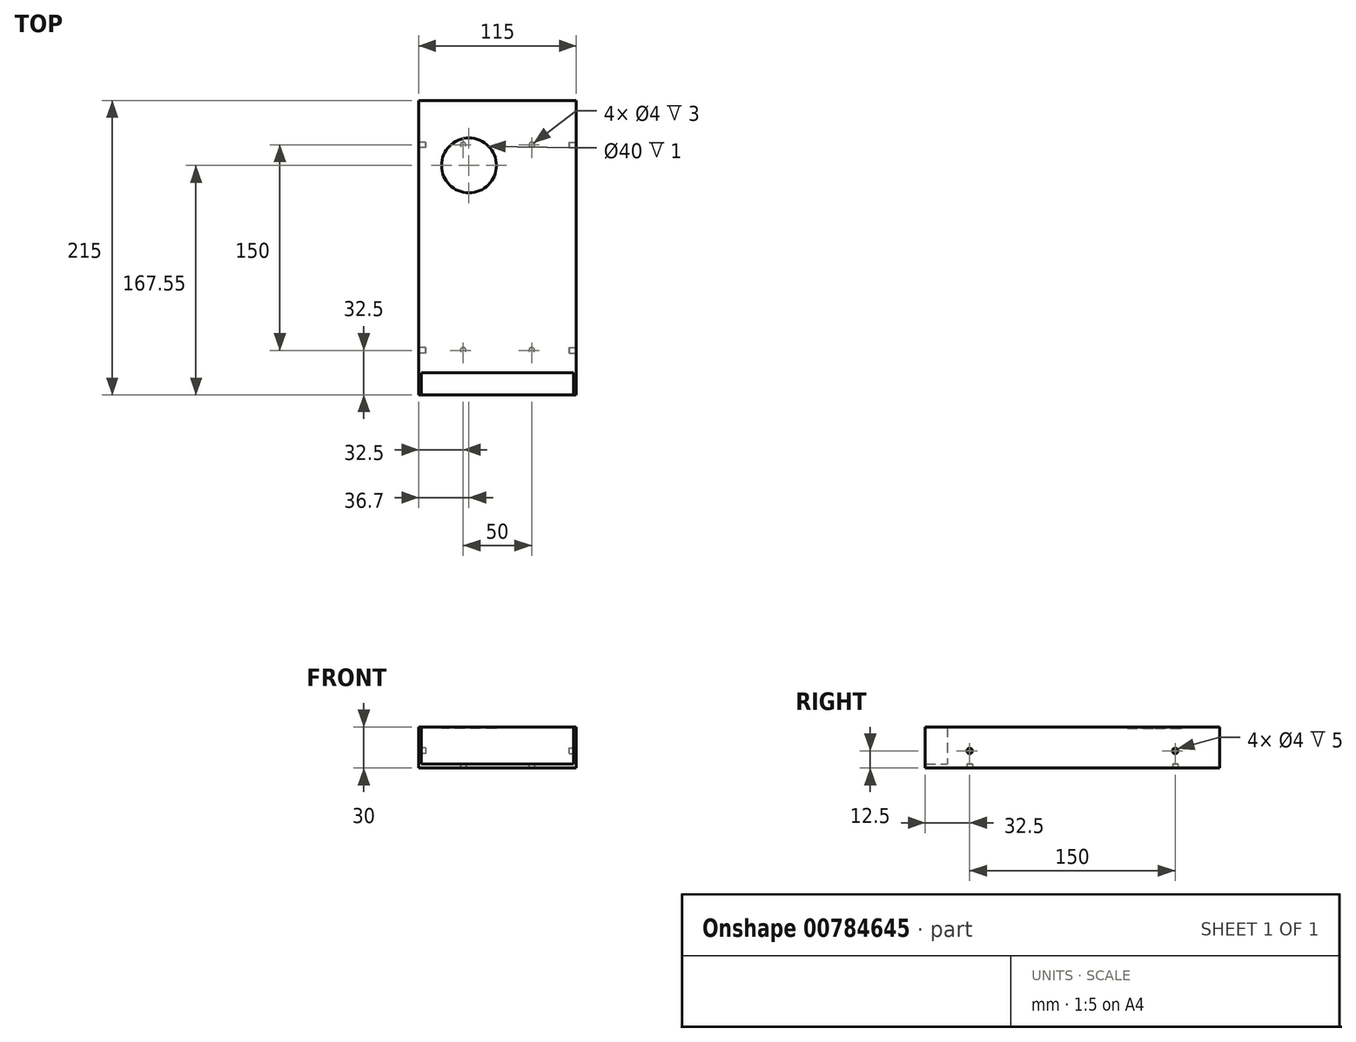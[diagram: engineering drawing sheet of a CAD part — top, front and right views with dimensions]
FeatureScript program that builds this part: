
annotation { "Feature Type Name" : "Feature", "Feature Type Description" : "" }
export const myFeature = defineFeature(function(context is Context, id is Id, definition is map)
    precondition{}
    {
        {
            var Q0;
            Q0=qCreatedBy(makeId("Top.planeOp"),FACE);
            var sketch = newSketch(context, id + "F0", { "sketchPlane" : qUnion([Q0])});
            skLineSegment(sketch, "E0.bottom", {"start": v(57.5, -107.5) * mm, "end": v(-57.5, -107.5) * mm});
            skLineSegment(sketch, "E0.top", {"start": v(57.5, 107.5) * mm, "end": v(-57.5, 107.5) * mm});
            skLineSegment(sketch, "E0.left", {"start": v(57.5, -107.5) * mm, "end": v(57.5, 107.5) * mm});
            skLineSegment(sketch, "E0.right", {"start": v(-57.5, -107.5) * mm, "end": v(-57.5, 107.5) * mm});
            skPoint(sketch, "E0.middle", {"position": v(0, 0) * mm});
            skLineSegment(sketch, "E1", {"start": v(-57.5, -91.25) * mm, "end": v(57.5, -91.25) * mm});
            skLineSegment(sketch, "E2", {"start": v(-55.5, -91.25) * mm, "end": v(-55.5, -107.5) * mm});
            skLineSegment(sketch, "E3", {"start": v(55.5, -91.25) * mm, "end": v(55.5, -107.5) * mm});
            skSolve(sketch);
        }
        {
            var Q0;
            Q0=makeQuery(id+"F0.imprint","IMPRINT",FACE,{"disambiguationData":[TD([[makeQuery(id+"F0.imprint","IMPRINT",EDGE,{"derivedFrom":sQuery(id+"F0.wireOp",EDGE,"E0.bottom")}),-1.0]])]});
            var Q1;
            {var subQ1=sQuery(id+"F0.wireOp",EDGE,"E0.top");Q1=makeQuery(id+"F0.imprint","IMPRINT",FACE,{"disambiguationData":[TD([[makeQuery(id+"F0.imprint","IMPRINT",EDGE,{"derivedFrom":subQ1}),1.0]])]});}
            extrude(context, id + "F1", {"entities" : qUnion([Q0, Q1]), "depth" : 3 * mm, "offsetDistance" : 25 * mm});
        }
        {
            var Q0;
            {var subQ3=sQuery(id+"F0.wireOp",EDGE,"E3");Q0=makeQuery(id+"F0.imprint","IMPRINT",FACE,{"disambiguationData":[TD([[makeQuery(id+"F0.imprint","IMPRINT",EDGE,{"derivedFrom":subQ3}),1.0]])]});}
            var Q1;
            {var subQ3=sQuery(id+"F0.wireOp",EDGE,"E2");Q1=makeQuery(id+"F0.imprint","IMPRINT",FACE,{"disambiguationData":[TD([[makeQuery(id+"F0.imprint","IMPRINT",EDGE,{"derivedFrom":subQ3}),-1.0]])]});}
            var Q2;
            {var subQ1=sQuery(id+"F0.wireOp",EDGE,"E0.top");Q2=makeQuery(id+"F0.imprint","IMPRINT",FACE,{"disambiguationData":[TD([[makeQuery(id+"F0.imprint","IMPRINT",EDGE,{"derivedFrom":subQ1}),1.0]])]});}
            extrude(context, id + "F2", {"entities" : qUnion([Q0, Q1, Q2]), "operationType" : NewBodyOperationType.ADD, "depth" : 30 * mm, "offsetDistance" : 25 * mm});
        }
        {
            var Q0;
            {var subQ0=sQuery(id+"F0.wireOp",EDGE,"E0.left");Q0=makeQuery(id+"F2.boolean.opBoolean","MERGE",FACE,{"derivedFrom":[makeQuery(id+"F1.opExtrude","SWEPT_FACE",FACE,{"disambiguationData":[OSD([subQ0])]}),makeQuery(id+"F2.opExtrude","SWEPT_FACE",FACE,{"disambiguationData":[OSD([subQ0])]})]});}
            var sketch = newSketch(context, id + "F3", { "sketchPlane" : qUnion([Q0])});
            skCircle(sketch, "E4", {"center": v(-75, 12.5) * mm, "radius": 2 * mm});
            skCircle(sketch, "E5", {"center": v(75, 12.5) * mm, "radius": 2 * mm});
            skSolve(sketch);
        }
        {
            var Q0;
            Q0 = qSketchRegion(id + "F3", true);
            extrude(context, id + "F4", {"entities" : qUnion([Q0]), "operationType" : NewBodyOperationType.REMOVE, "oppositeDirection" : true, "depth" : 5 * mm, "offsetDistance" : 25 * mm});
        }
        {
            var Q0;
            Q0=makeQuery(id+"F1.opExtrude","CAP_FACE",FACE,{"disambiguationData":[OSD([sQuery(id+"F0.wireOp",EDGE,"E0.bottom"),sQuery(id+"F0.wireOp",EDGE,"E0.top"),sQuery(id+"F0.wireOp",EDGE,"E0.left"),sQuery(id+"F0.wireOp",EDGE,"E0.right")])],"isStart":true});
            var sketch = newSketch(context, id + "F5", { "sketchPlane" : qUnion([Q0])});
            skCircle(sketch, "E6", {"center": v(25, 75) * mm, "radius": 2 * mm});
            skCircle(sketch, "E7", {"center": v(25, -75) * mm, "radius": 2 * mm});
            skPoint(sketch, "E8.0", {"position": v(57.5, 75) * mm});
            skPoint(sketch, "E9.0", {"position": v(57.5, -75) * mm});
            skCircle(sketch, "E10.MirrorC", {"center": v(-25, 75) * mm, "radius": 2 * mm});
            skCircle(sketch, "E11.MirrorC", {"center": v(-25, -75) * mm, "radius": 2 * mm});
            skSolve(sketch);
        }
        {
            var Q0;
            Q0 = qSketchRegion(id + "F5", true);
            extrude(context, id + "F6", {"entities" : qUnion([Q0]), "operationType" : NewBodyOperationType.REMOVE, "oppositeDirection" : true, "depth" : 3 * mm, "offsetDistance" : 25 * mm});
        }
        {
            var Q0;
            {var subQ0=sQuery(id+"F0.wireOp",EDGE,"E0.right");Q0=makeQuery(id+"F2.boolean.opBoolean","MERGE",FACE,{"derivedFrom":[makeQuery(id+"F1.opExtrude","SWEPT_FACE",FACE,{"disambiguationData":[OSD([subQ0])]}),makeQuery(id+"F2.opExtrude","SWEPT_FACE",FACE,{"disambiguationData":[OSD([subQ0])]})]});}
            var sketch = newSketch(context, id + "F7", { "sketchPlane" : qUnion([Q0])});
            skCircle(sketch, "E12", {"center": v(-75, 12.5) * mm, "radius": 2 * mm});
            skCircle(sketch, "E13", {"center": v(75, 12.5) * mm, "radius": 2 * mm});
            skSolve(sketch);
        }
        {
            var Q0;
            Q0 = qSketchRegion(id + "F7", true);
            extrude(context, id + "F8", {"entities" : qUnion([Q0]), "operationType" : NewBodyOperationType.REMOVE, "oppositeDirection" : true, "depth" : 5 * mm, "offsetDistance" : 25 * mm});
        }
        {
            var Q0;
            Q0=makeQuery(id+"F2.opExtrude","CAP_FACE",FACE,{"disambiguationData":[OSD([sQuery(id+"F0.wireOp",EDGE,"E0.bottom"),sQuery(id+"F0.wireOp",EDGE,"E0.top"),sQuery(id+"F0.wireOp",EDGE,"E0.left"),sQuery(id+"F0.wireOp",EDGE,"E0.right"),sQuery(id+"F0.wireOp",EDGE,"E1"),sQuery(id+"F0.wireOp",EDGE,"E2"),sQuery(id+"F0.wireOp",EDGE,"E3")])],"isStart":false});
            var sketch = newSketch(context, id + "F9", { "sketchPlane" : qUnion([Q0])});
            skCircle(sketch, "E14", {"center": v(-20.8, 60.05) * mm, "radius": 20 * mm});
            skSolve(sketch);
        }
        {
            var Q0;
            Q0 = qSketchRegion(id + "F9", true);
            extrude(context, id + "F10", {"entities" : qUnion([Q0]), "operationType" : NewBodyOperationType.REMOVE, "oppositeDirection" : true, "depth" : 1 * mm, "offsetDistance" : 25 * mm});
        }
    });
